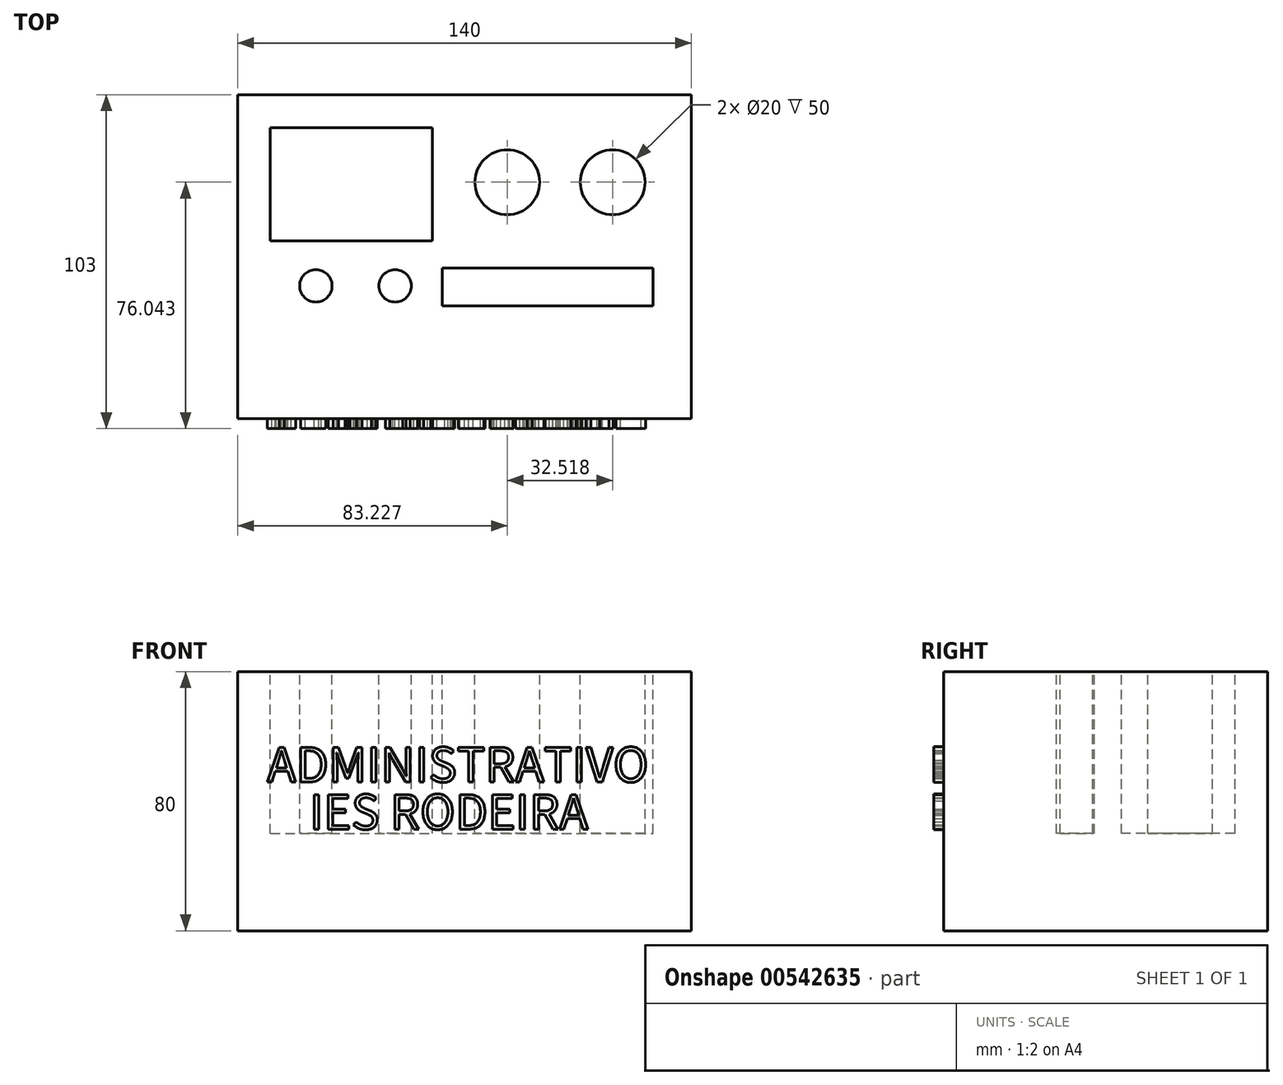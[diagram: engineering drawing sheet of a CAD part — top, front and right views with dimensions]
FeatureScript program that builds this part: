
annotation { "Feature Type Name" : "Feature", "Feature Type Description" : "" }
export const myFeature = defineFeature(function(context is Context, id is Id, definition is map)
    precondition{}
    {
        {
            var Q0;
            Q0=qCreatedBy(makeId("Top.planeOp"),FACE);
            var sketch = newSketch(context, id + "F0", { "sketchPlane" : qUnion([Q0])});
            skLineSegment(sketch, "E0.bottom", {"start": v(-31.61, 85.61) * mm, "end": v(108.39, 85.61) * mm});
            skLineSegment(sketch, "E0.top", {"start": v(-31.61, -14.39) * mm, "end": v(108.39, -14.39) * mm});
            skLineSegment(sketch, "E0.left", {"start": v(-31.61, 85.61) * mm, "end": v(-31.61, -14.39) * mm});
            skLineSegment(sketch, "E0.right", {"start": v(108.39, 85.61) * mm, "end": v(108.39, -14.39) * mm});
            skSolve(sketch);
        }
        {
            var Q0;
            Q0=makeQuery(id+"F0.imprint","IMPRINT",FACE,{"disambiguationData":[TD([[makeQuery(id+"F0.imprint","IMPRINT",EDGE,{"derivedFrom":sQuery(id+"F0.wireOp",EDGE,"E0.bottom")}),-1.0]])]});
            extrude(context, id + "F1", {"entities" : qUnion([Q0]), "depth" : 80 * mm, "offsetDistance" : 25 * mm});
        }
        {
            var Q0;
            Q0=makeQuery(id+"F1.opExtrude","CAP_FACE",FACE,{"disambiguationData":[OSD([sQuery(id+"F0.wireOp",EDGE,"E0.bottom"),sQuery(id+"F0.wireOp",EDGE,"E0.top"),sQuery(id+"F0.wireOp",EDGE,"E0.left"),sQuery(id+"F0.wireOp",EDGE,"E0.right")])],"isStart":false});
            var sketch = newSketch(context, id + "F2", { "sketchPlane" : qUnion([Q0])});
            skPoint(sketch, "E1", {"position": v(-31.61, 5.61) * mm});
            skPoint(sketch, "E2", {"position": v(-31.61, -14.39) * mm});
            skPoint(sketch, "E3", {"position": v(108.39, -14.39) * mm});
            skPoint(sketch, "E4", {"position": v(108.14, 85.57) * mm});
            skPoint(sketch, "E5", {"position": v(-31.61, 85.61) * mm});
            skLineSegment(sketch, "E6.bottom", {"start": v(-31.61, 13.62) * mm, "end": v(108.39, 13.62) * mm});
            skLineSegment(sketch, "E6.top", {"start": v(-31.61, 12.8) * mm, "end": v(108.39, 12.8) * mm});
            skLineSegment(sketch, "E6.left", {"start": v(-31.61, 13.62) * mm, "end": v(-31.61, 12.8) * mm});
            skLineSegment(sketch, "E6.right", {"start": v(108.39, 13.62) * mm, "end": v(108.39, 12.8) * mm});
            skPoint(sketch, "E7", {"position": v(-31.61, 66.52) * mm});
            skPoint(sketch, "E8", {"position": v(-13.91, 85.61) * mm});
            skLineSegment(sketch, "E9.bottom", {"start": v(-31.5, 85.52) * mm, "end": v(-21.5, 85.52) * mm});
            skLineSegment(sketch, "E9.left", {"start": v(-31.5, 85.52) * mm, "end": v(-31.5, 75.52) * mm});
            skLineSegment(sketch, "E10.bottom", {"start": v(108.14, 85.57) * mm, "end": v(98.14, 85.57) * mm});
            skLineSegment(sketch, "E10.left", {"start": v(108.14, 85.57) * mm, "end": v(108.14, 75.57) * mm});
            skLineSegment(sketch, "E11.bottom", {"start": v(-21.5, 75.52) * mm, "end": v(28.5, 75.52) * mm});
            skLineSegment(sketch, "E11.top", {"start": v(-21.5, 40.52) * mm, "end": v(28.5, 40.52) * mm});
            skLineSegment(sketch, "E11.left", {"start": v(-21.5, 75.52) * mm, "end": v(-21.5, 40.52) * mm});
            skLineSegment(sketch, "E11.right", {"start": v(28.5, 75.52) * mm, "end": v(28.5, 40.52) * mm});
            skCircle(sketch, "E12", {"center": v(51.62, 58.65) * mm, "radius": 10 * mm});
            skCircle(sketch, "E13", {"center": v(84.14, 58.65) * mm, "radius": 10 * mm});
            skCircle(sketch, "E14", {"center": v(-7.44, 26.66) * mm, "radius": 5 * mm});
            skCircle(sketch, "E15", {"center": v(17.02, 26.66) * mm, "radius": 5 * mm});
            skPoint(sketch, "E16.center.orphan", {"position": v(38.39, 26.66) * mm});
            skLineSegment(sketch, "E17.bottom", {"start": v(31.59, 32.12) * mm, "end": v(96.62, 32.12) * mm});
            skLineSegment(sketch, "E17.top", {"start": v(31.59, 20.41) * mm, "end": v(96.62, 20.41) * mm});
            skLineSegment(sketch, "E17.left", {"start": v(31.59, 32.12) * mm, "end": v(31.59, 20.41) * mm});
            skLineSegment(sketch, "E17.right", {"start": v(96.62, 32.12) * mm, "end": v(96.62, 20.41) * mm});
            skPoint(sketch, "E18.orphan", {"position": v(-31.61, 26.66) * mm});
            skPoint(sketch, "E19.trimOffspring.end.orphan", {"position": v(108.39, 26.66) * mm});
            skSolve(sketch);
        }
        {
            var Q0;
            Q0=sQuery(id+"F2.wireOp",EDGE,"E6.bottom");
            extrude(context, id + "F3", {"bodyType" : ToolBodyType.SURFACE, "surfaceEntities" : qUnion([Q0]), "depth" : -5 * mm, "offsetDistance" : 25 * mm});
        }
        {
            var Q0;
            Q0=makeQuery(id+"F2.imprint","IMPRINT",FACE,{"disambiguationData":[TD([[makeQuery(id+"F2.imprint","IMPRINT",EDGE,{"derivedFrom":sQuery(id+"F2.wireOp",EDGE,"E11.bottom")}),-1.0]])]});
            var Q1;
            Q1=makeQuery(id+"F2.imprint","IMPRINT",FACE,{"disambiguationData":[TD([[makeQuery(id+"F2.imprint","IMPRINT",EDGE,{"derivedFrom":sQuery(id+"F2.wireOp",EDGE,"E12")}),1.0]])]});
            var Q2;
            Q2=makeQuery(id+"F2.imprint","IMPRINT",FACE,{"disambiguationData":[TD([[makeQuery(id+"F2.imprint","IMPRINT",EDGE,{"derivedFrom":sQuery(id+"F2.wireOp",EDGE,"E13")}),1.0]])]});
            var Q3;
            Q3=makeQuery(id+"F2.imprint","IMPRINT",FACE,{"disambiguationData":[TD([[makeQuery(id+"F2.imprint","IMPRINT",EDGE,{"derivedFrom":sQuery(id+"F2.wireOp",EDGE,"E14")}),1.0]])]});
            var Q4;
            Q4=makeQuery(id+"F2.imprint","IMPRINT",FACE,{"disambiguationData":[TD([[makeQuery(id+"F2.imprint","IMPRINT",EDGE,{"derivedFrom":sQuery(id+"F2.wireOp",EDGE,"E15")}),1.0]])]});
            var Q5;
            Q5=makeQuery(id+"F2.imprint","IMPRINT",FACE,{"disambiguationData":[TD([[makeQuery(id+"F2.imprint","IMPRINT",EDGE,{"derivedFrom":sQuery(id+"F2.wireOp",EDGE,"E17.bottom")}),-1.0]])]});
            extrude(context, id + "F4", {"entities" : qUnion([Q0, Q1, Q2, Q3, Q4, Q5]), "operationType" : NewBodyOperationType.REMOVE, "depth" : -50 * mm, "offsetDistance" : 25 * mm});
        }
        {
            var Q0;
            Q0=makeQuery(id+"F1.opExtrude","SWEPT_FACE",FACE,{"disambiguationData":[OSD([sQuery(id+"F0.wireOp",EDGE,"E0.top")])]});
            var sketch = newSketch(context, id + "F5", { "sketchPlane" : qUnion([Q0])});
            skText(sketch, "E20", { "text": "ADMINISTRATIVO\n    IES RODEIRA", "fontName": "NotoSansCJKjp-Regular.otf"});
            const initialGuessF5  = {"E20": [-0.02244, 0.04593, 1, 0, 0.0105]};
            skSetInitialGuess(sketch, initialGuessF5);
            skSolve(sketch);
        }
        {
            var Q0;
            Q0=qSketchRegion(id+"F5",true);
            extrude(context, id + "F6", {"entities" : qUnion([Q0]), "operationType" : NewBodyOperationType.ADD, "depth" : 3 * mm, "offsetDistance" : 25 * mm});
        }
    });
